# Revit family: Building-RicaricaVeicoliElettrici-GEWISS-JOINON-ION_PAVIMENTO-EV-R
name_source: partatom
category: Apparecchi elettrici
units: mm (PartAtom-declared; Revit-internal decimal feet)

## family parameters
Basato su piano di lavoro = No
Condiviso = No
Mantenere orientamento annotazione = No
Numero OmniClass = 23.80.00.00
Punto di calcolo locali = Sì
Quota connettore circolare = Usa diametro
Sempre verticale = Sì
Taglio con vuoti quando caricato = No
Tipo di parte = Normale
Titolo OmniClass = Electric Power and Lighting

## types (1)
- Building-RicaricaVeicoliElettrici-GEWISS-JOINON-ION_PAVIMENTO-EV-R
    Attivazione ricarica = Gestito da remoto, via OCPP 1.6J
    C = a=b
    Caratteristiche meccaniche = -
    Colore = Grigio, Testata RAL 7011
    Comunicazione = Kit Ethernet e Modem 4G con antenna di potenziamento
    Connettività: = LAN, WIFI, 4G
    Contatore di energia = SI (Tipo MID)
    Corpo = Corpo
    Corrente erogata (max) = 32 A per socket (10 A per Tipo F)
    Corrente nominale: = 64 Ampere
    DC Leakage check = Non necessario
    Descrizione = COL. JOINON RFID 22 KW 2XT2S+SC 3G EV-R
    Grado di protezione = IP54
    H1 = 1550 mm  [stored 5.0853 ft]
    Human Interface = LED RGB e TFT Display
    IDF = 2821c7d1-cd63-47cd-9342-b4f1b15777c0
    INPUT: = -
    Immagine tipo = ION_PAVIM.jpg
    Laterali = Laterali
    Lettore RFID = Si
    Materiale = Lamiera d'acciaio
    Modello = GWJ1023W100
    Morsettiera: = 5 x 35 mm²
    N. Prese Tipo 2 = 2 (+2 prese domestiche tipo F)
    Numero di prese (tipo) = 2 (Tipo 2 anti-vandalo,  con shutter) + 2 (Tipo F)
    OUTPUT : = -
    Personalizzabile: = SI (frontale)
    Potenza complessiva: = 44 Chilowatt
    Potenza di ricarica = 22 kW + 22 kW
    Potenza max. = 22 kW per socket (2,3 kW per Tipo F)
    Produttore = GEWISS S.p.A.
    Protezione magnetotermica = 40A - 4P - Curva D
    Protezioni = Magnetotermico + Diff. Tipo B
    Resistenza agli urti = IK10
    Riarmo protezioni da remoto = No
    Temperatura di utilizzo = -25 +50 °C
    Tensione nominale = 400 Volt
    Tensione nominale di isolamento (Ui) = 400 Volt
    Testa = Testa
    Tipo di installazione e montaggio = A pavimento
    Tipo di protezione differenziale = 40 A - 4P - Tipo B
    Trattamento esterno = Anti-corrosione ed anti-graffito
    URL = https://www.gewiss.com
    Versione file RFA = 19.4
    ang1 = 62.22°
    h2 = 1392 mm
    r2 = 79.00°
    r4 = 18.00°

note: [stored X ft] marks values corroborated as IEEE doubles in the binary element streams (Revit-internal decimal feet)
